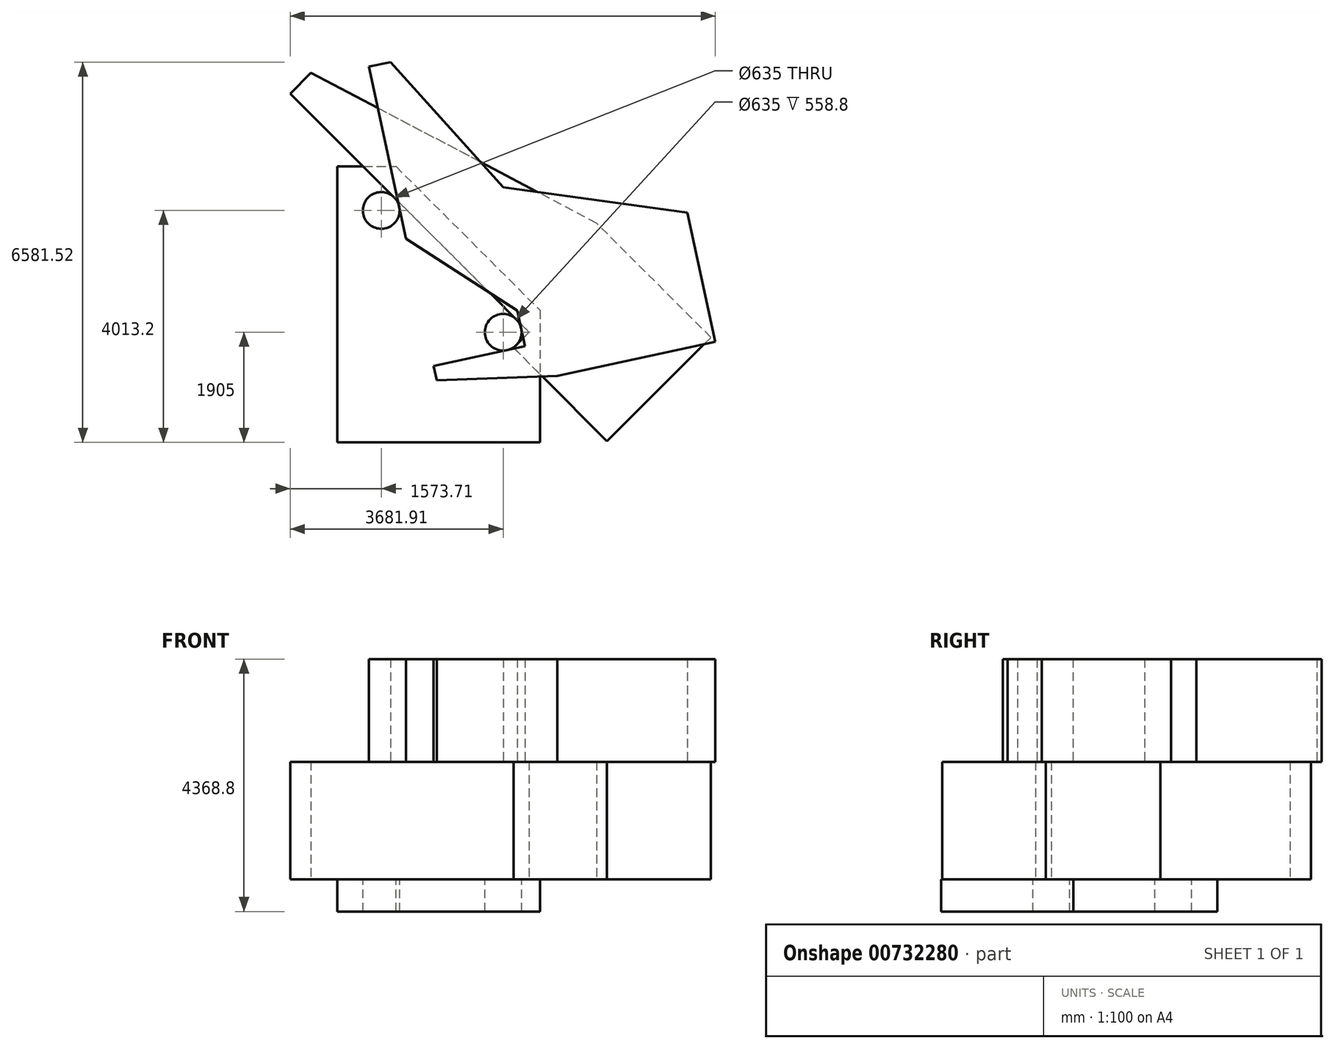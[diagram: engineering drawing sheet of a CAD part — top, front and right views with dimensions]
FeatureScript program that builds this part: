
annotation { "Feature Type Name" : "Feature", "Feature Type Description" : "" }
export const myFeature = defineFeature(function(context is Context, id is Id, definition is map)
    precondition{}
    {
        {
            var Q0;
            Q0=qCreatedBy(makeId("Top.planeOp"),FACE);
            var sketch = newSketch(context, id + "F0", { "sketchPlane" : qUnion([Q0])});
            skLineSegment(sketch, "E0.bottom", {"start": v(-3505.2, 15240) * mm, "end": v(0, 15240) * mm});
            skLineSegment(sketch, "E0.top", {"start": v(-3505.2, 0) * mm, "end": v(0, 0) * mm});
            skLineSegment(sketch, "E0.left", {"start": v(-3505.2, 15240) * mm, "end": v(-3505.2, 0) * mm});
            skLineSegment(sketch, "E0.right", {"start": v(0, 15240) * mm, "end": v(0, 0) * mm});
            skLineSegment(sketch, "E1", {"start": v(-3505.2, 5791.2) * mm, "end": v(0, 2286) * mm});
            skLineSegment(sketch, "E2", {"start": v(-3505.2, 8890) * mm, "end": v(0, 8890) * mm});
            skLineSegment(sketch, "E3", {"start": v(-3505.2, 4775.2) * mm, "end": v(-2489.2, 4775.2) * mm});
            skLineSegment(sketch, "E4", {"start": v(-508, 2794) * mm, "end": v(0, 2794) * mm});
            skCircle(sketch, "E5", {"center": v(-2743.2, 4013.2) * mm, "radius": 317.5 * mm});
            skCircle(sketch, "E6", {"center": v(-635, 1905) * mm, "radius": 317.5 * mm});
            skLineSegment(sketch, "E7", {"start": v(-3505.2, 0) * mm, "end": v(-4572, 0) * mm});
            skLineSegment(sketch, "E8", {"start": v(-4572, 0) * mm, "end": v(-4572, 15240) * mm});
            skLineSegment(sketch, "E9", {"start": v(-4572, 15240) * mm, "end": v(-3505.2, 15240) * mm});
            skLineSegment(sketch, "E10", {"start": v(-3505.2, 4013.2) * mm, "end": v(-4572, 4013.2) * mm});
            skLineSegment(sketch, "E11", {"start": v(-3505.2, 4775.2) * mm, "end": v(-859.5, 2129.5) * mm, "construction": true});
            skSolve(sketch);
        }
        {
            var Q0;
            {var subQ5=sQuery(id+"F0.wireOp",EDGE,"E2");Q0=makeQuery(id+"F0.imprint","IMPRINT",FACE,{"disambiguationData":[TD([[makeQuery(id+"F0.imprint","IMPRINT",EDGE,{"derivedFrom":subQ5}),-1.0]])]});}
            var sketch = newSketch(context, id + "F1", { "sketchPlane" : qUnion([Q0])});
            skLineSegment(sketch, "E12", {"start": v(-4316.9, 6035.92) * mm, "end": v(-185.99, 1905) * mm});
            skLineSegment(sketch, "E13", {"start": v(-185.99, 1905) * mm, "end": v(-455.4, 1635.6) * mm});
            skLineSegment(sketch, "E14", {"start": v(-455.4, 1635.6) * mm, "end": v(1161.05, 19.15) * mm});
            skLineSegment(sketch, "E15", {"start": v(1161.05, 19.15) * mm, "end": v(2957.1, 1815.2) * mm});
            skLineSegment(sketch, "E16", {"start": v(2957.1, 1815.2) * mm, "end": v(981.45, 3790.85) * mm});
            skLineSegment(sketch, "E17", {"start": v(981.45, 3790.85) * mm, "end": v(-3957.7, 6395.13) * mm});
            skLineSegment(sketch, "E18", {"start": v(-3957.7, 6395.13) * mm, "end": v(-4316.9, 6035.92) * mm});
            skSolve(sketch);
        }
        {
            var Q0;
            {var subQ1=sQuery(id+"F0.wireOp",EDGE,"E0.top");Q0=makeQuery(id+"F0.imprint","IMPRINT",FACE,{"disambiguationData":[TD([[makeQuery(id+"F0.imprint","IMPRINT",EDGE,{"derivedFrom":subQ1}),1.0]])]});}
            extrude(context, id + "F2", {"entities" : qUnion([Q0]), "oppositeDirection" : true, "depth" : 558.8 * mm, "offsetDistance" : 25.4 * mm});
        }
        {
            var Q0;
            Q0=sQuery(id+"F0.wireOp",EDGE,"E6");
            var Q1;
            Q1=sQuery(id+"F0.wireOp",EDGE,"E5");
            extrude(context, id + "F3", {"bodyType" : ToolBodyType.SURFACE, "surfaceEntities" : qUnion([Q0, Q1]), "depth" : 25400 * mm, "offsetDistance" : 25.4 * mm});
        }
        {
            var Q0;
            Q0 = qSketchRegion(id + "F1", true);
            extrude(context, id + "F4", {"entities" : qUnion([Q0]), "operationType" : NewBodyOperationType.ADD, "depth" : 2032 * mm, "offsetDistance" : 25.4 * mm});
        }
        {
            var Q0;
            Q0=makeQuery(id+"F4.opExtrude","CAP_FACE",FACE,{"disambiguationData":[OSD([sQuery(id+"F1.wireOp",EDGE,"E12"),sQuery(id+"F1.wireOp",EDGE,"E13"),sQuery(id+"F1.wireOp",EDGE,"E14"),sQuery(id+"F1.wireOp",EDGE,"E15"),sQuery(id+"F1.wireOp",EDGE,"E16"),sQuery(id+"F1.wireOp",EDGE,"E17"),sQuery(id+"F1.wireOp",EDGE,"E18")])],"isStart":false});
            var sketch = newSketch(context, id + "F5", { "sketchPlane" : qUnion([Q0])});
            skLineSegment(sketch, "E19", {"start": v(-1837.84, 1320.83) * mm, "end": v(-257.7, 1661.56) * mm});
            skLineSegment(sketch, "E20", {"start": v(-257.7, 1661.56) * mm, "end": v(-391.56, 2282.3) * mm});
            skLineSegment(sketch, "E21", {"start": v(-391.56, 2282.3) * mm, "end": v(-2312.42, 3521.69) * mm});
            skLineSegment(sketch, "E22", {"start": v(-2312.42, 3521.69) * mm, "end": v(-2954.9, 6501.2) * mm});
            skLineSegment(sketch, "E23", {"start": v(-2954.9, 6501.2) * mm, "end": v(-2582.46, 6581.52) * mm});
            skLineSegment(sketch, "E24", {"start": v(2550, 3975.07) * mm, "end": v(3031.87, 1740.43) * mm});
            skLineSegment(sketch, "E25", {"start": v(3031.87, 1740.43) * mm, "end": v(300.64, 1151.49) * mm});
            skLineSegment(sketch, "E26", {"start": v(300.64, 1151.49) * mm, "end": v(-1784.3, 1072.54) * mm});
            skLineSegment(sketch, "E27", {"start": v(-1784.3, 1072.54) * mm, "end": v(-1837.84, 1320.83) * mm});
            skLineSegment(sketch, "E28", {"start": v(-2582.46, 6581.52) * mm, "end": v(-630.34, 4415.91) * mm});
            skLineSegment(sketch, "E29", {"start": v(-630.34, 4415.91) * mm, "end": v(2550, 3975.07) * mm});
            skSolve(sketch);
        }
        {
            var Q0;
            Q0 = qSketchRegion(id + "F5", true);
            extrude(context, id + "F6", {"entities" : qUnion([Q0]), "operationType" : NewBodyOperationType.ADD, "depth" : 1778 * mm, "offsetDistance" : 25.4 * mm});
        }
    });
